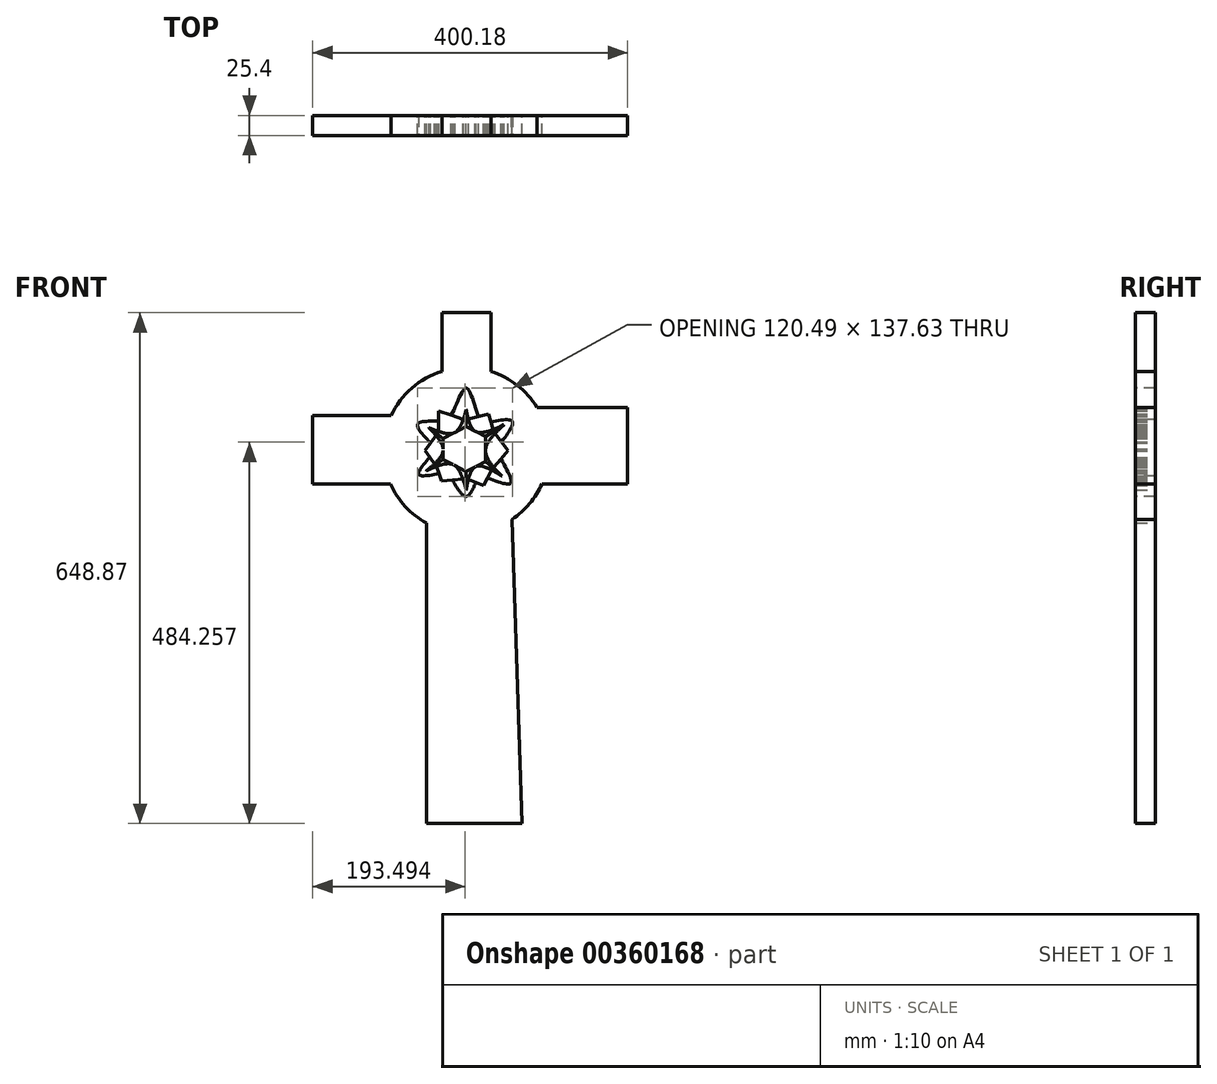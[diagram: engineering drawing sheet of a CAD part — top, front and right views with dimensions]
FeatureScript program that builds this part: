
annotation { "Feature Type Name" : "Feature", "Feature Type Description" : "" }
export const myFeature = defineFeature(function(context is Context, id is Id, definition is map)
    precondition{}
    {
        {
            var Q0;
            Q0=qCreatedBy(makeId("Front.planeOp"),FACE);
            var sketch = newSketch(context, id + "F0", { "sketchPlane" : qUnion([Q0])});
            skLineSegment(sketch, "E0", {"start": v(0, 0) * mm, "end": v(0, 30.37) * mm});
            skLineSegment(sketch, "E1", {"start": v(0, 30.37) * mm, "end": v(-29.4, 15.18) * mm});
            skPoint(sketch, "E1.endSnap0", {"position": v(0, 15.18) * mm});
            skLineSegment(sketch, "E2", {"start": v(-29.4, 15.18) * mm, "end": v(-29.4, -11.33) * mm});
            skLineSegment(sketch, "E3", {"start": v(-29.4, -11.33) * mm, "end": v(0, -26.75) * mm});
            skLineSegment(sketch, "E4", {"start": v(0, -26.75) * mm, "end": v(24.61, -14.04) * mm});
            skLineSegment(sketch, "E5", {"start": v(24.61, -14.04) * mm, "end": v(24.61, 17.6) * mm});
            skLineSegment(sketch, "E6", {"start": v(24.61, 17.6) * mm, "end": v(0, 30.37) * mm});
            skLineSegment(sketch, "E7", {"start": v(0, 30.37) * mm, "end": v(0, 52.05) * mm});
            skLineSegment(sketch, "E8", {"start": v(-29.4, 15.18) * mm, "end": v(-47.48, 28.92) * mm});
            skLineSegment(sketch, "E9", {"start": v(-29.4, -11.33) * mm, "end": v(-50.6, -25.79) * mm});
            skLineSegment(sketch, "E10", {"start": v(0, -26.75) * mm, "end": v(0, -50.37) * mm});
            skLineSegment(sketch, "E11", {"start": v(24.61, -14.04) * mm, "end": v(45.3, -32.53) * mm});
            skLineSegment(sketch, "E12", {"start": v(24.61, 17.6) * mm, "end": v(48.2, 32.78) * mm});
            skFitSpline(sketch, "E13", {"points": [v(0, 52.05) * mm, v(-14.7, 22.77) * mm, v(-47.48, 28.92) * mm], "startDerivative": vector(-20.64, -76.5) * mm, "endDerivative": vector(-74.24, 30.08) * mm});
            skFitSpline(sketch, "E14", {"points": [v(-47.48, 28.92) * mm, v(-29.4, 0) * mm, v(-50.6, -25.79) * mm], "startDerivative": vector(55.71, -58.96) * mm, "endDerivative": vector(-62.19, -50.43) * mm});
            skFitSpline(sketch, "E15", {"points": [v(-50.6, -25.79) * mm, v(-16.5, -18.1) * mm, v(0, -50.37) * mm], "startDerivative": vector(77.8, 35.2) * mm, "endDerivative": vector(23.57, -84.02) * mm});
            skFitSpline(sketch, "E16", {"points": [v(0, -50.37) * mm, v(12.3, -20.4) * mm, v(45.3, -32.53) * mm], "startDerivative": vector(15.44, 82) * mm, "endDerivative": vector(74.77, -45.47) * mm});
            skFitSpline(sketch, "E17", {"points": [v(45.3, -32.53) * mm, v(24.61, 0) * mm, v(48.2, 32.78) * mm], "startDerivative": vector(-63.74, 66.08) * mm, "endDerivative": vector(69.01, 64.54) * mm});
            skFitSpline(sketch, "E18", {"points": [v(48.2, 32.78) * mm, v(12.3, 23.98) * mm, v(0, 52.05) * mm], "startDerivative": vector(-79.77, -36.62) * mm, "endDerivative": vector(-15.63, 76.95) * mm});
            skLineSegment(sketch, "E19", {"start": v(-35.05, 23.88) * mm, "end": v(-35.05, 50.37) * mm});
            skLineSegment(sketch, "E20", {"start": v(-35.05, 50.37) * mm, "end": v(-3.42, 39.36) * mm});
            skLineSegment(sketch, "E21", {"start": v(2.48, 39.83) * mm, "end": v(28.68, 46.51) * mm});
            skLineSegment(sketch, "E22", {"start": v(28.68, 46.51) * mm, "end": v(34.28, 26.39) * mm});
            skLineSegment(sketch, "E23", {"start": v(36.56, 21.9) * mm, "end": v(53.26, 0) * mm});
            skLineSegment(sketch, "E24", {"start": v(53.26, 0) * mm, "end": v(34.8, -21.65) * mm});
            skLineSegment(sketch, "E25", {"start": v(2.52, -36.98) * mm, "end": v(21.93, -44.58) * mm});
            skLineSegment(sketch, "E26", {"start": v(21.93, -44.58) * mm, "end": v(32.6, -24.8) * mm});
            skLineSegment(sketch, "E27", {"start": v(-37.76, -19.97) * mm, "end": v(-31.09, -39.04) * mm});
            skLineSegment(sketch, "E28", {"start": v(-31.09, -39.04) * mm, "end": v(-3.96, -36.24) * mm});
            skLineSegment(sketch, "E29", {"start": v(-40.3, -17.43) * mm, "end": v(-52.18, 0) * mm});
            skLineSegment(sketch, "E30", {"start": v(-52.18, 0) * mm, "end": v(-38.14, 19.04) * mm});
            skFitSpline(sketch, "E31", {"points": [v(-19.24, 44.86) * mm, v(0, 79.31) * mm, v(15.58, 43.17) * mm], "startDerivative": vector(39.85, 64.2) * mm, "endDerivative": vector(29.75, -67.95) * mm});
            skFitSpline(sketch, "E32", {"points": [v(-45.16, 9.52) * mm, v(-61.7, 33.26) * mm, v(-35.05, 37.13) * mm], "startDerivative": vector(-54.56, 56.5) * mm, "endDerivative": vector(75.56, -1.64) * mm});
            skFitSpline(sketch, "E33", {"points": [v(-46.24, -8.71) * mm, v(-60.25, -30.37) * mm, v(-34.42, -29.5) * mm], "startDerivative": vector(-47.94, -54.58) * mm, "endDerivative": vector(71.55, 12.98) * mm});
            skFitSpline(sketch, "E34", {"points": [v(-17.53, -37.64) * mm, v(0, -58.32) * mm, v(12.23, -40.78) * mm], "startDerivative": vector(34.97, -59.26) * mm, "endDerivative": vector(24.32, 55.24) * mm});
            skFitSpline(sketch, "E35", {"points": [v(27.26, -34.7) * mm, v(56.4, -41.45) * mm, v(44.03, -10.82) * mm], "startDerivative": vector(80.2, -31.81) * mm, "endDerivative": vector(-45.6, 78.64) * mm});
            skFitSpline(sketch, "E36", {"points": [v(44.91, 10.95) * mm, v(58.56, 36.87) * mm, v(31.48, 36.45) * mm], "startDerivative": vector(47.68, 64.03) * mm, "endDerivative": vector(-75.35, -13.54) * mm});
            skLineSegment(sketch, "E37", {"start": v(-107.14, 0) * mm, "end": v(-52.18, 0) * mm});
            skLineSegment(sketch, "E38", {"start": v(0, -58.32) * mm, "end": v(0, -119.7) * mm});
            skLineSegment(sketch, "E39", {"start": v(53.26, 0) * mm, "end": v(110.13, 0) * mm});
            skCircle(sketch, "E40", {"center": v(0, 0) * mm, "radius": 105.1 * mm});
            skPoint(sketch, "E41.0.midPoint", {"position": v(0, 137.31) * mm});
            skLineSegment(sketch, "E42", {"start": v(-30.67, 100.54) * mm, "end": v(-30.67, 175.11) * mm});
            skLineSegment(sketch, "E43", {"start": v(-30.67, 175.11) * mm, "end": v(31.48, 175.11) * mm});
            skLineSegment(sketch, "E44", {"start": v(31.48, 175.11) * mm, "end": v(31.48, 100.28) * mm});
            skLineSegment(sketch, "E45", {"start": v(-95.42, 44.08) * mm, "end": v(-195.04, 44.08) * mm});
            skLineSegment(sketch, "E46", {"start": v(-195.04, 44.08) * mm, "end": v(-195.04, -42.38) * mm});
            skLineSegment(sketch, "E47", {"start": v(-195.04, -42.38) * mm, "end": v(-96.19, -42.38) * mm});
            skLineSegment(sketch, "E48", {"start": v(89.77, 54.68) * mm, "end": v(205.14, 54.68) * mm});
            skLineSegment(sketch, "E49", {"start": v(205.14, 54.68) * mm, "end": v(205.14, -42.38) * mm});
            skLineSegment(sketch, "E50", {"start": v(205.14, -42.38) * mm, "end": v(96.19, -42.38) * mm});
            skLineSegment(sketch, "E51", {"start": v(-50.26, -92.31) * mm, "end": v(-50.26, -473.76) * mm});
            skLineSegment(sketch, "E52", {"start": v(-50.26, -473.76) * mm, "end": v(71.1, -473.76) * mm});
            skLineSegment(sketch, "E53", {"start": v(71.1, -473.76) * mm, "end": v(58.24, -87.5) * mm});
            skSolve(sketch);
        }
        {
            var Q0;
            Q0=makeQuery(id+"F0.imprint","IMPRINT",FACE,{"disambiguationData":[TD([[makeQuery(id+"F0.imprint","IMPRINT",EDGE,{"derivedFrom":sQuery(id+"F0.wireOp",EDGE,"E1")}),1.0]])]});
            extrude(context, id + "F1", {"entities" : qUnion([Q0]), "depth" : 25.4 * mm});
        }
        {
            var Q0;
            {var subQ0=sQuery(id+"F0.wireOp",EDGE,"E8");Q0=makeQuery(id+"F0.imprint","IMPRINT",FACE,{"disambiguationData":[TD([[makeQuery(id+"F0.imprint","IMPRINT",EDGE,{"derivedFrom":subQ0}),-1.0]])]});}
            var Q1;
            {var subQ0=sQuery(id+"F0.wireOp",EDGE,"E7");Q1=makeQuery(id+"F0.imprint","IMPRINT",FACE,{"disambiguationData":[TD([[makeQuery(id+"F0.imprint","IMPRINT",EDGE,{"derivedFrom":subQ0}),1.0]])]});}
            var Q2;
            {var subQ0=sQuery(id+"F0.wireOp",EDGE,"E7");Q2=makeQuery(id+"F0.imprint","IMPRINT",FACE,{"disambiguationData":[TD([[makeQuery(id+"F0.imprint","IMPRINT",EDGE,{"derivedFrom":subQ0}),-1.0]])]});}
            var Q3;
            {var subQ0=sQuery(id+"F0.wireOp",EDGE,"E12");Q3=makeQuery(id+"F0.imprint","IMPRINT",FACE,{"disambiguationData":[TD([[makeQuery(id+"F0.imprint","IMPRINT",EDGE,{"derivedFrom":subQ0}),1.0]])]});}
            var Q4;
            {var subQ0=sQuery(id+"F0.wireOp",EDGE,"E12");Q4=makeQuery(id+"F0.imprint","IMPRINT",FACE,{"disambiguationData":[TD([[makeQuery(id+"F0.imprint","IMPRINT",EDGE,{"derivedFrom":subQ0}),-1.0]])]});}
            var Q5;
            {var subQ0=sQuery(id+"F0.wireOp",EDGE,"E11");Q5=makeQuery(id+"F0.imprint","IMPRINT",FACE,{"disambiguationData":[TD([[makeQuery(id+"F0.imprint","IMPRINT",EDGE,{"derivedFrom":subQ0}),1.0]])]});}
            var Q6;
            {var subQ0=sQuery(id+"F0.wireOp",EDGE,"E11");Q6=makeQuery(id+"F0.imprint","IMPRINT",FACE,{"disambiguationData":[TD([[makeQuery(id+"F0.imprint","IMPRINT",EDGE,{"derivedFrom":subQ0}),-1.0]])]});}
            var Q7;
            {var subQ0=sQuery(id+"F0.wireOp",EDGE,"E10");Q7=makeQuery(id+"F0.imprint","IMPRINT",FACE,{"disambiguationData":[TD([[makeQuery(id+"F0.imprint","IMPRINT",EDGE,{"derivedFrom":subQ0}),1.0]])]});}
            var Q8;
            {var subQ0=sQuery(id+"F0.wireOp",EDGE,"E10");Q8=makeQuery(id+"F0.imprint","IMPRINT",FACE,{"disambiguationData":[TD([[makeQuery(id+"F0.imprint","IMPRINT",EDGE,{"derivedFrom":subQ0}),-1.0]])]});}
            var Q9;
            {var subQ0=sQuery(id+"F0.wireOp",EDGE,"E9");Q9=makeQuery(id+"F0.imprint","IMPRINT",FACE,{"disambiguationData":[TD([[makeQuery(id+"F0.imprint","IMPRINT",EDGE,{"derivedFrom":subQ0}),1.0]])]});}
            var Q10;
            {var subQ0=sQuery(id+"F0.wireOp",EDGE,"E9");Q10=makeQuery(id+"F0.imprint","IMPRINT",FACE,{"disambiguationData":[TD([[makeQuery(id+"F0.imprint","IMPRINT",EDGE,{"derivedFrom":subQ0}),-1.0]])]});}
            var Q11;
            {var subQ0=sQuery(id+"F0.wireOp",EDGE,"E8");Q11=makeQuery(id+"F0.imprint","IMPRINT",FACE,{"disambiguationData":[TD([[makeQuery(id+"F0.imprint","IMPRINT",EDGE,{"derivedFrom":subQ0}),1.0]])]});}
            extrude(context, id + "F2", {"entities" : qUnion([Q0, Q1, Q2, Q3, Q4, Q5, Q6, Q7, Q8, Q9, Q10, Q11]), "depth" : 25.4 * mm});
        }
        {
            var Q0;
            {var subQ3=sQuery(id+"F0.wireOp",EDGE,"E13");var subQ5=sQuery(id+"F0.wireOp",EDGE,"E1");var subQ8=makeQuery(id+"F0.imprint","INTERSECT",VERTEX,{"disambiguationData":[OD(0.0)],"derivedFrom":[subQ5,subQ3]});Q0=makeQuery(id+"F0.imprint","IMPRINT",FACE,{"disambiguationData":[TD([[makeQuery(id+"F0.imprint","IMPRINT",EDGE,{"disambiguationData":[TD([[subQ8,-1.0]])],"derivedFrom":subQ5}),-1.0]])]});}
            var Q1;
            {var subQ1=sQuery(id+"F0.wireOp",EDGE,"E18");var subQ3=sQuery(id+"F0.wireOp",EDGE,"E6");var subQ7=makeQuery(id+"F0.imprint","INTERSECT",VERTEX,{"disambiguationData":[OD(0.0)],"derivedFrom":[subQ3,subQ1]});Q1=makeQuery(id+"F0.imprint","IMPRINT",FACE,{"disambiguationData":[TD([[makeQuery(id+"F0.imprint","IMPRINT",EDGE,{"disambiguationData":[TD([[subQ7,-1.0]])],"derivedFrom":subQ3}),-1.0]])]});}
            var Q2;
            {var subQ1=sQuery(id+"F0.wireOp",EDGE,"E17");var subQ3=sQuery(id+"F0.wireOp",EDGE,"E5");var subQ8=makeQuery(id+"F0.imprint","INTERSECT",VERTEX,{"disambiguationData":[OD(0.0)],"derivedFrom":[subQ3,subQ1]});Q2=makeQuery(id+"F0.imprint","IMPRINT",FACE,{"disambiguationData":[TD([[makeQuery(id+"F0.imprint","IMPRINT",EDGE,{"disambiguationData":[TD([[subQ8,-1.0]])],"derivedFrom":subQ3}),-1.0]])]});}
            var Q3;
            {var subQ1=sQuery(id+"F0.wireOp",EDGE,"E14");var subQ3=sQuery(id+"F0.wireOp",EDGE,"E2");var subQ8=makeQuery(id+"F0.imprint","INTERSECT",VERTEX,{"disambiguationData":[OD(0.0)],"derivedFrom":[subQ3,subQ1]});Q3=makeQuery(id+"F0.imprint","IMPRINT",FACE,{"disambiguationData":[TD([[makeQuery(id+"F0.imprint","IMPRINT",EDGE,{"disambiguationData":[TD([[subQ8,-1.0]])],"derivedFrom":subQ3}),-1.0]])]});}
            var Q4;
            {var subQ1=sQuery(id+"F0.wireOp",EDGE,"E15");var subQ3=sQuery(id+"F0.wireOp",EDGE,"E3");var subQ4=makeQuery(id+"F0.imprint","INTERSECT",VERTEX,{"disambiguationData":[OD(0.0)],"derivedFrom":[subQ3,subQ1]});Q4=makeQuery(id+"F0.imprint","IMPRINT",FACE,{"disambiguationData":[TD([[makeQuery(id+"F0.imprint","IMPRINT",EDGE,{"disambiguationData":[TD([[subQ4,-1.0]])],"derivedFrom":subQ3}),-1.0]])]});}
            var Q5;
            {var subQ1=sQuery(id+"F0.wireOp",EDGE,"E16");var subQ3=sQuery(id+"F0.wireOp",EDGE,"E4");var subQ8=makeQuery(id+"F0.imprint","INTERSECT",VERTEX,{"disambiguationData":[OD(0.0)],"derivedFrom":[subQ3,subQ1]});Q5=makeQuery(id+"F0.imprint","IMPRINT",FACE,{"disambiguationData":[TD([[makeQuery(id+"F0.imprint","IMPRINT",EDGE,{"disambiguationData":[TD([[subQ8,-1.0]])],"derivedFrom":subQ3}),-1.0]])]});}
            extrude(context, id + "F3", {"entities" : qUnion([Q0, Q1, Q2, Q3, Q4, Q5]), "depth" : 25.4 * mm});
        }
        {
            var Q0;
            {var subQ0=sQuery(id+"F0.wireOp",EDGE,"E31");Q0=makeQuery(id+"F0.imprint","IMPRINT",FACE,{"disambiguationData":[TD([[makeQuery(id+"F0.imprint","IMPRINT",EDGE,{"derivedFrom":subQ0}),-1.0]])]});}
            var Q1;
            {var subQ0=sQuery(id+"F0.wireOp",EDGE,"E32");Q1=makeQuery(id+"F0.imprint","IMPRINT",FACE,{"disambiguationData":[TD([[makeQuery(id+"F0.imprint","IMPRINT",EDGE,{"derivedFrom":subQ0}),-1.0]])]});}
            var Q2;
            {var subQ0=sQuery(id+"F0.wireOp",EDGE,"E33");Q2=makeQuery(id+"F0.imprint","IMPRINT",FACE,{"disambiguationData":[TD([[makeQuery(id+"F0.imprint","IMPRINT",EDGE,{"derivedFrom":subQ0}),1.0]])]});}
            var Q3;
            {var subQ0=sQuery(id+"F0.wireOp",EDGE,"E34");Q3=makeQuery(id+"F0.imprint","IMPRINT",FACE,{"disambiguationData":[TD([[makeQuery(id+"F0.imprint","IMPRINT",EDGE,{"derivedFrom":subQ0}),1.0]])]});}
            var Q4;
            {var subQ0=sQuery(id+"F0.wireOp",EDGE,"E35");Q4=makeQuery(id+"F0.imprint","IMPRINT",FACE,{"disambiguationData":[TD([[makeQuery(id+"F0.imprint","IMPRINT",EDGE,{"derivedFrom":subQ0}),1.0]])]});}
            var Q5;
            {var subQ0=sQuery(id+"F0.wireOp",EDGE,"E36");Q5=makeQuery(id+"F0.imprint","IMPRINT",FACE,{"disambiguationData":[TD([[makeQuery(id+"F0.imprint","IMPRINT",EDGE,{"derivedFrom":subQ0}),1.0]])]});}
            extrude(context, id + "F4", {"entities" : qUnion([Q0, Q1, Q2, Q3, Q4, Q5]), "depth" : 25.4 * mm});
        }
        {
            var Q0;
            {var subQ5=sQuery(id+"F0.wireOp",EDGE,"E31");Q0=makeQuery(id+"F0.imprint","IMPRINT",FACE,{"disambiguationData":[TD([[makeQuery(id+"F0.imprint","IMPRINT",EDGE,{"derivedFrom":subQ5}),1.0]])]});}
            var Q1;
            {var subQ0=sQuery(id+"F0.wireOp",EDGE,"E33");Q1=makeQuery(id+"F0.imprint","IMPRINT",FACE,{"disambiguationData":[TD([[makeQuery(id+"F0.imprint","IMPRINT",EDGE,{"derivedFrom":subQ0}),-1.0]])]});}
            var Q2;
            {var subQ3=sQuery(id+"F0.wireOp",EDGE,"E35");Q2=makeQuery(id+"F0.imprint","IMPRINT",FACE,{"disambiguationData":[TD([[makeQuery(id+"F0.imprint","IMPRINT",EDGE,{"derivedFrom":subQ3}),-1.0]])]});}
            extrude(context, id + "F5", {"entities" : qUnion([Q0, Q1, Q2]), "depth" : 25.4 * mm});
        }
        {
            var Q0;
            {var subQ0=sQuery(id+"F0.wireOp",EDGE,"E42");Q0=makeQuery(id+"F0.imprint","IMPRINT",FACE,{"disambiguationData":[TD([[makeQuery(id+"F0.imprint","IMPRINT",EDGE,{"derivedFrom":subQ0}),-1.0]])]});}
            var Q1;
            {var subQ0=sQuery(id+"F0.wireOp",EDGE,"E45");Q1=makeQuery(id+"F0.imprint","IMPRINT",FACE,{"disambiguationData":[TD([[makeQuery(id+"F0.imprint","IMPRINT",EDGE,{"derivedFrom":subQ0}),1.0]])]});}
            var Q2;
            {var subQ0=sQuery(id+"F0.wireOp",EDGE,"E48");Q2=makeQuery(id+"F0.imprint","IMPRINT",FACE,{"disambiguationData":[TD([[makeQuery(id+"F0.imprint","IMPRINT",EDGE,{"derivedFrom":subQ0}),-1.0]])]});}
            var Q3;
            {var subQ0=sQuery(id+"F0.wireOp",EDGE,"E51");Q3=makeQuery(id+"F0.imprint","IMPRINT",FACE,{"disambiguationData":[TD([[makeQuery(id+"F0.imprint","IMPRINT",EDGE,{"derivedFrom":subQ0}),1.0]])]});}
            extrude(context, id + "F6", {"entities" : qUnion([Q0, Q1, Q2, Q3]), "operationType" : NewBodyOperationType.ADD, "depth" : 25.4 * mm});
        }
    });
